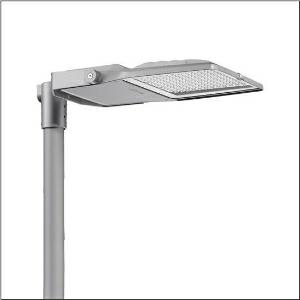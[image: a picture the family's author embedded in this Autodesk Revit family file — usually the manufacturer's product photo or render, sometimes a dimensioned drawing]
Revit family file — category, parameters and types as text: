
# Revit family: floodlight_fl_21_midi___pl43_5xa7786e4a3a_aacc
name_source: partatom
category: Lighting Fixtures
units: mm (PartAtom-declared; Revit-internal decimal feet)

## family parameters
Cut with Voids When Loaded = No
Host = Face
Light Source = No
Part Type = Normal
Room Calculation Point = No
Round Connector Dimension = Use Diameter
Shared = No

## types (1)
- --- (1 x LED, 28830 lm, 212.4 W, 4000K)
    Apparent Load = 212 VA
    CIE Flux Codes = 27 78 99 100 100
    Color Rendering = 70
    Color Temperature = 4000K
    Default Elevation = 1800 mm
    Description = Floodlight FL 21 midi, floodlight, primary light control with lens, of PMMA, primary optical cover: protective disc, of toughened safety glass, transparent, light distribution: PL43, light emission: direct distribution, installation type: surface-mounted, LED, High Power LED, rated luminous flux: 28.830lm, luminous efficacy: 136lm/W, light colour: 740, colour temperature: 4000K, control gear: Smart Interface (Zhaga)D4i, control: overheat protection, constant luminous flux control, time-dependent luminous flux control, flexible luminous flux parameterisation, pre-setting: logarithmic dimming characteristic, with terminal, 6-pole, mains connection: 220..240V, AC, 50/60Hz, start of lifetime: 212W, end of service life: 231W, reduction: 95W, mast bracket, of diecast aluminium, powder-coated, Siteco® metallic grey (DB 702S), corrosivity category C5 mid according to DIN EN ISO 12944, suitable for swimming pools, chlorine-resistant, sealing non-destructively replaceable, mast bracket, of steel, galvanised, powder-coated, Siteco® metallic grey (DB 702S), Smart Interface below and above, protection rating (complete): IP66, insulation class (complete): insulation class II (safety insulation), certification: CE, ENEC, VDE, protection symbol: D, impact resistance: IK08, permissible operating ambient temperature: -40..+40°C, permissible operating ambient temperature for outdoor applications: -40..+50°C, standard: DIN EN 12944, LABS conformity tested according to VDMA 24364:2018-05, packaging unit: 1 piece

Light Distribution: PL43
    Height = 76 mm
    Lamp = 1 x LED
    Lamp Light Flux = 28830 lm
    Lamp Power = 212.4 W
    Lamp count = 1
    Length = 657 mm
    Luminous efficacy = 136 lm/W
    Manufacturer = Siteco
    ModVariant = No
    Model = 5XA7786E4A3A
    Number of Poles = 1
    OnlyDefault = Yes
    Power Factor = 1
    Product Name = Floodlight FL 21 midi | PL43
    Product group = floodlight | pylon annexe
    ProductGroupID = 6200
    Protection Class = Protection class II
    Protection Degree = IP 66
    RLX_Detail_Level = 1
    RLX_Emergency_Light_Flux = 0 lm
    RLX_Emergency_Type = 0
    RLX_Emergency_Type_DB = No
    RlxData = <blob elided: 104537 chars, md5=becfa2dd>
    Socket = socket
    Standby Power = 0 W
    System Light Flux = 28830 lm
    System Power = 212 W
    Type Comments = factory setting: luminous flux: 100 % | dim-lin: 254 | 710 mA
    Type Image = l_1007123.jpg
    URL = http://relux.com
    VarID = @adj_089180
    Voltage = 0 V
    Weight = 0.00 kg
    Width = 442 mm

## geometry (parser evidence)
native form markers: Blend x4, Sweep x12
no freeform markers — native parametric forms only
